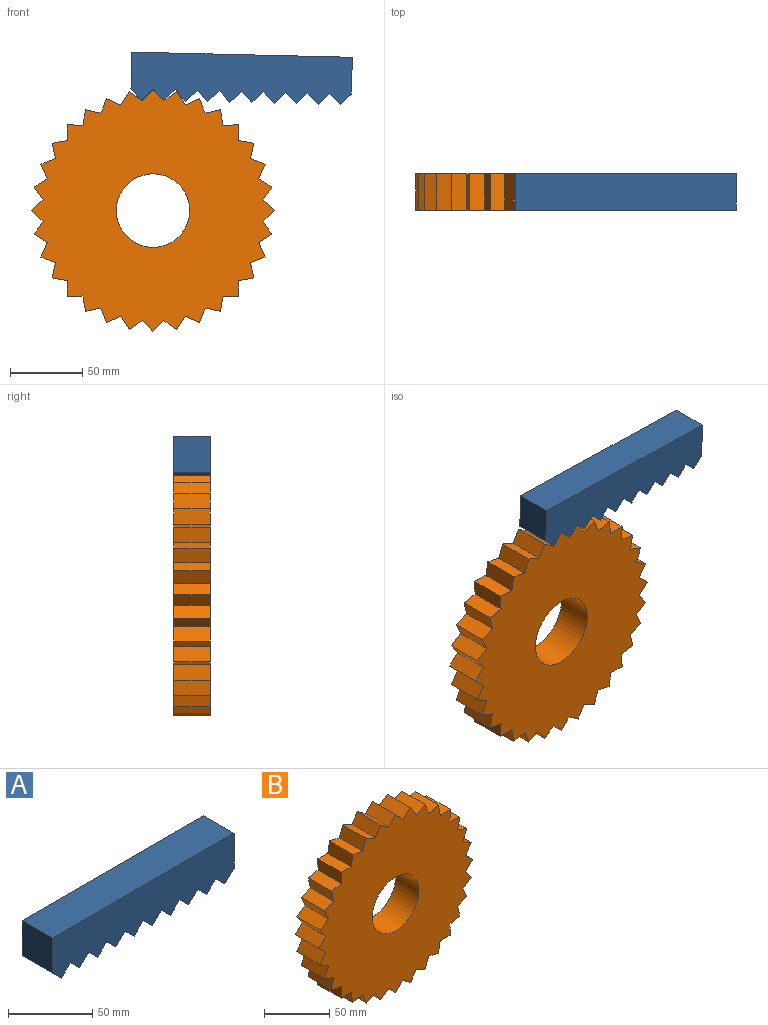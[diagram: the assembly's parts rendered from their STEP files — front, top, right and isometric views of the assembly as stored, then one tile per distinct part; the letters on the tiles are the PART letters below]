
ASSEMBLY  parts=2 mates=1
PART A: 25 faces, bbox 152.4x25.4x33 mm
  f0: plane 25.4x7.62mm, normal (0.71,0,-0.71), area 273.7mm2, adj f1,f22,f23,f24
  f1: plane 25.4x25.4mm, normal (1,0,0), area 645.2mm2, adj f0,f2,f23,f24
  f2: plane 152.4x25.4mm, normal (0,0,1), area 3871mm2, adj f1,f3,f23,f24
  f3: plane 25.4x25.4mm, normal (-1,0,0), area 645.2mm2, adj f2,f4,f23,f24
  f4: plane 25.4x7.62mm, normal (-0.71,0,-0.71), area 273.7mm2, adj f3,f5,f23,f24
  f5: plane 25.4x7.62mm, normal (0.71,0,-0.71), area 273.7mm2, adj f4,f6,f23,f24
  f6: plane 25.4x7.62mm, normal (-0.71,0,-0.71), area 273.7mm2, adj f5,f7,f23,f24
  f7: plane 25.4x7.62mm, normal (0.71,0,-0.71), area 273.7mm2, adj f6,f8,f23,f24
  f8: plane 25.4x7.62mm, normal (-0.71,0,-0.71), area 273.7mm2, adj f7,f9,f23,f24
  f9: plane 25.4x7.62mm, normal (0.71,0,-0.71), area 273.7mm2, adj f8,f10,f23,f24
  f10: plane 25.4x7.62mm, normal (-0.71,0,-0.71), area 273.7mm2, adj f9,f11,f23,f24
  f11: plane 25.4x7.62mm, normal (0.71,0,-0.71), area 273.7mm2, adj f10,f12,f23,f24
  f12: plane 25.4x7.62mm, normal (-0.71,0,-0.71), area 273.7mm2, adj f11,f13,f23,f24
  f13: plane 25.4x7.62mm, normal (0.71,0,-0.71), area 273.7mm2, adj f12,f14,f23,f24
  f14: plane 25.4x7.62mm, normal (-0.71,0,-0.71), area 273.7mm2, adj f13,f15,f23,f24
  f15: plane 25.4x7.62mm, normal (0.71,0,-0.71), area 273.7mm2, adj f14,f16,f23,f24
  f16: plane 25.4x7.62mm, normal (-0.71,0,-0.71), area 273.7mm2, adj f15,f17,f23,f24
  f17: plane 25.4x7.62mm, normal (0.71,0,-0.71), area 273.7mm2, adj f16,f18,f23,f24
  f18: plane 25.4x7.62mm, normal (-0.71,0,-0.71), area 273.7mm2, adj f17,f19,f23,f24
  f19: plane 25.4x7.62mm, normal (0.71,0,-0.71), area 273.7mm2, adj f18,f20,f23,f24
  f20: plane 25.4x7.62mm, normal (-0.71,0,-0.71), area 273.7mm2, adj f19,f21,f23,f24
  f21: plane 25.4x7.62mm, normal (0.71,0,-0.71), area 273.7mm2, adj f20,f22,f23,f24
  f22: plane 25.4x7.62mm, normal (-0.71,0,-0.71), area 273.7mm2, adj f0,f21,f23,f24
  f23: plane 152.4x33.02mm, normal (0,-1,0), area 4451.6mm2, adj f0,f1,f2,f3,f4,f5,f6,f7
  f24: plane 152.4x33.02mm, normal (0,1,0), area 4451.6mm2, adj f0,f1,f2,f3,f4,f5,f6,f7
PART B: 67 faces, bbox 167.6x25.4x167.6 mm
  f0: cylinder r=25.4mm len=50.8mm, axis (0,1,0), area 4053.7mm2, adj f1,f2
  f1: plane 167.64x167.64mm, normal (0,-1,0), area 18041mm2, adj f0,f3,f4,f5,f6,f7,f8,f9
  f2: plane 167.64x167.64mm, normal (0,1,0), area 18041mm2, adj f0,f3,f4,f5,f6,f7,f8,f9
  f3: plane 25.4x7.86mm, normal (0.69,0,0.72), area 275.3mm2, adj f1,f2,f4,f66
  f4: plane 25.4x8.89mm, normal (0.82,0,-0.57), area 275.9mm2, adj f1,f2,f3,f5
  f5: plane 25.4x9.16mm, normal (0.53,0,0.85), area 275.3mm2, adj f1,f2,f4,f6
  f6: plane 25.4x9.93mm, normal (0.91,0,-0.4), area 275.9mm2, adj f1,f2,f5,f7
  f7: plane 25.4x10.11mm, normal (0.36,0,0.93), area 275.3mm2, adj f1,f2,f6,f8
  f8: plane 25.4x10.6mm, normal (0.98,0,-0.22), area 275.9mm2, adj f1,f2,f7,f9
  f9: plane 25.4x10.68mm, normal (0.17,0,0.99), area 275.3mm2, adj f1,f2,f8,f10
  f10: plane 25.4x10.86mm, normal (1,0,-0.02), area 275.9mm2, adj f1,f2,f9,f11
  f11: plane 25.4x10.83mm, normal (-0.03,0,1), area 275.3mm2, adj f1,f2,f10,f12
  f12: plane 25.4x10.7mm, normal (0.99,0,0.17), area 275.9mm2, adj f1,f2,f11,f13
  f13: plane 25.4x10.57mm, normal (-0.22,0,0.98), area 275.3mm2, adj f1,f2,f12,f14
  f14: plane 25.4x10.13mm, normal (0.93,0,0.36), area 275.9mm2, adj f1,f2,f13,f15
  f15: plane 25.4x9.9mm, normal (-0.41,0,0.91), area 275.3mm2, adj f1,f2,f14,f16
  f16: plane 25.4x9.17mm, normal (0.84,0,0.54), area 275.9mm2, adj f1,f2,f15,f17
  f17: plane 25.4x8.86mm, normal (-0.58,0,0.82), area 275.3mm2, adj f1,f2,f16,f18
  f18: plane 25.4x7.86mm, normal (0.72,0,0.69), area 275.9mm2, adj f1,f2,f17,f19
  f19: plane 25.4x7.86mm, normal (-0.72,0,0.69), area 275.3mm2, adj f1,f2,f18,f20
  f20: plane 25.4x8.89mm, normal (0.57,0,0.82), area 275.9mm2, adj f1,f2,f19,f21
  f21: plane 25.4x9.16mm, normal (-0.85,0,0.53), area 275.3mm2, adj f1,f2,f20,f22
  f22: plane 25.4x9.93mm, normal (0.4,0,0.91), area 275.9mm2, adj f1,f2,f21,f23
  f23: plane 25.4x10.11mm, normal (-0.93,0,0.36), area 275.3mm2, adj f1,f2,f22,f24
  f24: plane 25.4x10.6mm, normal (0.22,0,0.98), area 275.9mm2, adj f1,f2,f23,f25
  f25: plane 25.4x10.68mm, normal (-0.99,0,0.17), area 275.3mm2, adj f1,f2,f24,f26
  f26: plane 25.4x10.86mm, normal (0.02,0,1), area 275.9mm2, adj f1,f2,f25,f27
  f27: plane 25.4x10.83mm, normal (-1,0,-0.03), area 275.3mm2, adj f1,f2,f26,f28
  f28: plane 25.4x10.7mm, normal (-0.17,0,0.99), area 275.9mm2, adj f1,f2,f27,f29
  f29: plane 25.4x10.57mm, normal (-0.98,0,-0.22), area 275.3mm2, adj f1,f2,f28,f30
  f30: plane 25.4x10.13mm, normal (-0.36,0,0.93), area 275.9mm2, adj f1,f2,f29,f31
  f31: plane 25.4x9.9mm, normal (-0.91,0,-0.41), area 275.3mm2, adj f1,f2,f30,f32
  f32: plane 25.4x9.17mm, normal (-0.54,0,0.84), area 275.9mm2, adj f1,f2,f31,f33
  f33: plane 25.4x8.86mm, normal (-0.82,0,-0.58), area 275.3mm2, adj f1,f2,f32,f34
  f34: plane 25.4x7.86mm, normal (-0.69,0,0.72), area 275.9mm2, adj f1,f2,f33,f35
  f35: plane 25.4x7.86mm, normal (-0.69,0,-0.72), area 275.3mm2, adj f1,f2,f34,f36
  f36: plane 25.4x8.89mm, normal (-0.82,0,0.57), area 275.9mm2, adj f1,f2,f35,f37
  f37: plane 25.4x9.16mm, normal (-0.53,0,-0.85), area 275.3mm2, adj f1,f2,f36,f38
  f38: plane 25.4x9.93mm, normal (-0.91,0,0.4), area 275.9mm2, adj f1,f2,f37,f39
  f39: plane 25.4x10.11mm, normal (-0.36,0,-0.93), area 275.3mm2, adj f1,f2,f38,f40
  f40: plane 25.4x10.6mm, normal (-0.98,0,0.22), area 275.9mm2, adj f1,f2,f39,f41
  f41: plane 25.4x10.68mm, normal (-0.17,0,-0.99), area 275.3mm2, adj f1,f2,f40,f42
  f42: plane 25.4x10.86mm, normal (-1,0,0.02), area 275.9mm2, adj f1,f2,f41,f43
  f43: plane 25.4x10.83mm, normal (0.03,0,-1), area 275.3mm2, adj f1,f2,f42,f44
  f44: plane 25.4x10.7mm, normal (-0.99,0,-0.17), area 275.9mm2, adj f1,f2,f43,f45
  f45: plane 25.4x10.57mm, normal (0.22,0,-0.98), area 275.3mm2, adj f1,f2,f44,f46
  f46: plane 25.4x10.13mm, normal (-0.93,0,-0.36), area 275.9mm2, adj f1,f2,f45,f47
  f47: plane 25.4x9.9mm, normal (0.41,0,-0.91), area 275.3mm2, adj f1,f2,f46,f48
  f48: plane 25.4x9.17mm, normal (-0.84,0,-0.54), area 275.9mm2, adj f1,f2,f47,f49
  f49: plane 25.4x8.86mm, normal (0.58,0,-0.82), area 275.3mm2, adj f1,f2,f48,f50
  f50: plane 25.4x7.86mm, normal (-0.72,0,-0.69), area 275.9mm2, adj f1,f2,f49,f51
  f51: plane 25.4x7.86mm, normal (0.72,0,-0.69), area 275.3mm2, adj f1,f2,f50,f52
  f52: plane 25.4x8.89mm, normal (-0.57,0,-0.82), area 275.9mm2, adj f1,f2,f51,f53
  f53: plane 25.4x9.16mm, normal (0.85,0,-0.53), area 275.3mm2, adj f1,f2,f52,f54
  f54: plane 25.4x9.93mm, normal (-0.4,0,-0.91), area 275.9mm2, adj f1,f2,f53,f55
  f55: plane 25.4x10.11mm, normal (0.93,0,-0.36), area 275.3mm2, adj f1,f2,f54,f56
  f56: plane 25.4x10.6mm, normal (-0.22,0,-0.98), area 275.9mm2, adj f1,f2,f55,f57
  f57: plane 25.4x10.68mm, normal (0.99,0,-0.17), area 275.3mm2, adj f1,f2,f56,f58
  f58: plane 25.4x10.86mm, normal (-0.02,0,-1), area 275.9mm2, adj f1,f2,f57,f59
  f59: plane 25.4x10.83mm, normal (1,0,0.03), area 275.3mm2, adj f1,f2,f58,f60
  f60: plane 25.4x10.7mm, normal (0.17,0,-0.99), area 275.9mm2, adj f1,f2,f59,f61
  f61: plane 25.4x10.57mm, normal (0.98,0,0.22), area 275.3mm2, adj f1,f2,f60,f62
  f62: plane 25.4x10.13mm, normal (0.36,0,-0.93), area 275.9mm2, adj f1,f2,f61,f63
  f63: plane 25.4x9.9mm, normal (0.91,0,0.41), area 275.3mm2, adj f1,f2,f62,f64
  f64: plane 25.4x9.17mm, normal (0.54,0,-0.84), area 275.9mm2, adj f1,f2,f63,f65
  f65: plane 25.4x8.86mm, normal (0.82,0,0.58), area 275.3mm2, adj f1,f2,f64,f66
  f66: plane 25.4x7.86mm, normal (0.69,0,-0.72), area 275.9mm2, adj f1,f2,f3,f65
PLACE A rot(axis=(0,1,0),1.3deg) t=(61.27,0,95.05)mm
PLACE B at identity
MATE fastened A.f6 <-> B.f18  axis (-0.72,0,-0.69) through (3.75,-12.7,79.89)mm
